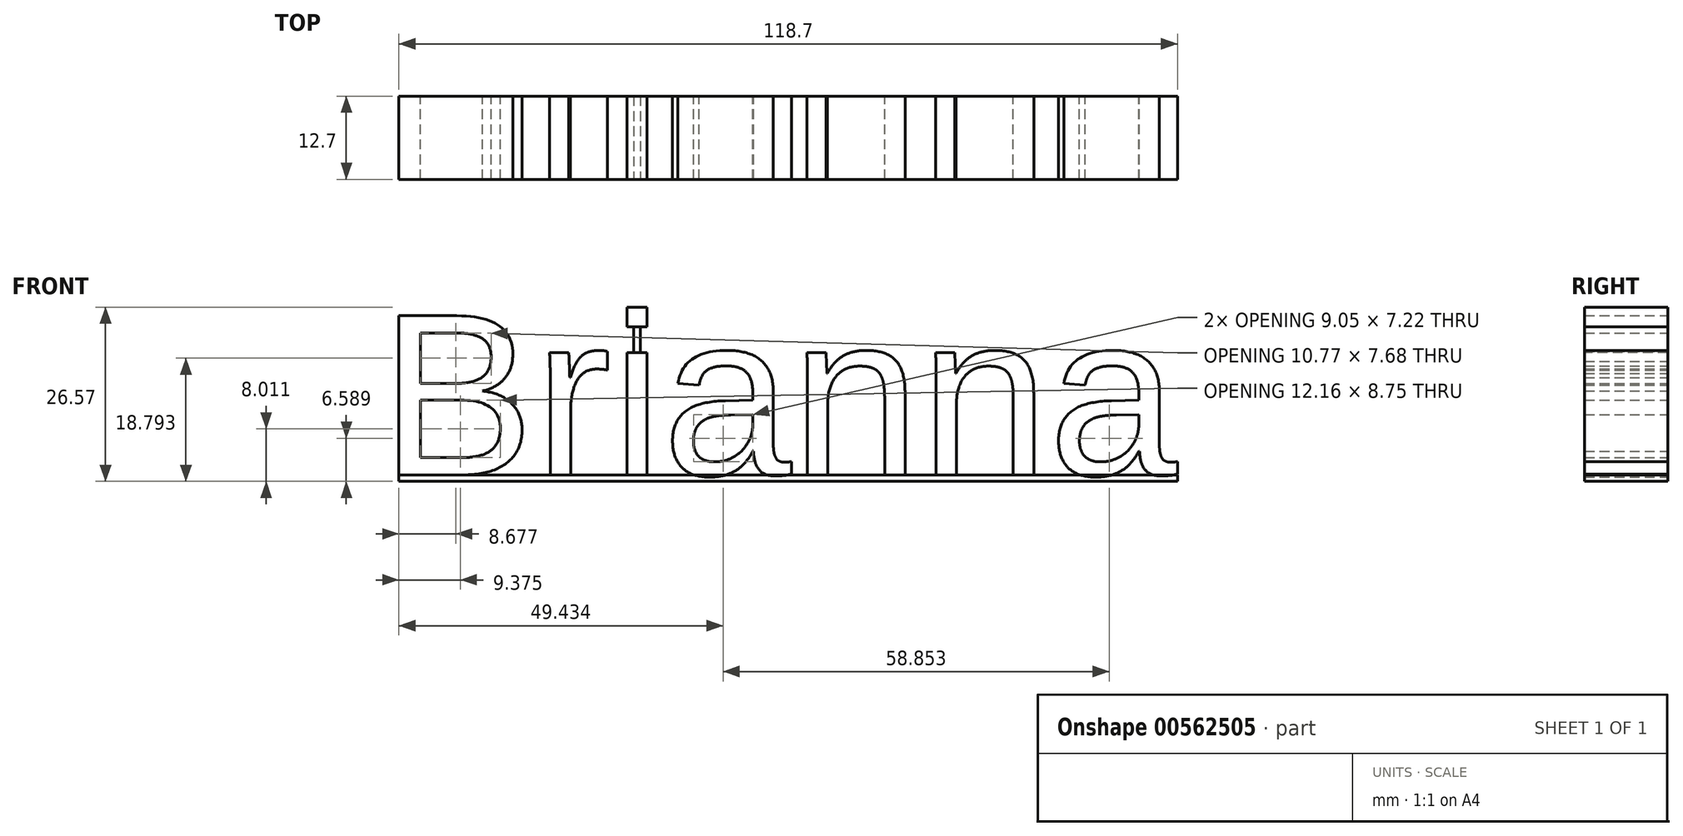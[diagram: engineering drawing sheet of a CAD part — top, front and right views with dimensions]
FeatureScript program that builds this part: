
annotation { "Feature Type Name" : "Feature", "Feature Type Description" : "" }
export const myFeature = defineFeature(function(context is Context, id is Id, definition is map)
    precondition{}
    {
        {
            var Q0;
            Q0=qCreatedBy(makeId("Front.planeOp"),FACE);
            var sketch = newSketch(context, id + "F0", { "sketchPlane" : qUnion([Q0])});
            skText(sketch, "E0", { "text": "Brianna", "fontName": "Arimo-Regular.ttf"});
            skPoint(sketch, "E1", {"position": v(0, 12.7) * mm});
            const initialGuessF0  = {"E0": [-0.06202, 0, 1, 0, 0.0254]};
            skSetInitialGuess(sketch, initialGuessF0);
            skSolve(sketch);
        }
        {
            var Q0;
            Q0=qSketchRegion(id+"F0",true);
            extrude(context, id + "F1", {"entities" : qUnion([Q0]), "endBound" : BoundingType.SYMMETRIC, "depth" : 12.7 * mm, "offsetDistance" : 25.4 * mm});
        }
        {
            var Q0;
            Q0=qCreatedBy(makeId("Top.planeOp"),FACE);
            var sketch = newSketch(context, id + "F2", { "sketchPlane" : qUnion([Q0])});
            skPoint(sketch, "E2.0", {"position": v(-59.12, 0) * mm});
            skLineSegment(sketch, "E3.0", {"start": v(-59.12, -6.35) * mm, "end": v(-59.12, 6.35) * mm});
            skLineSegment(sketch, "E4.0", {"start": v(59.57, -6.35) * mm, "end": v(59.57, 6.35) * mm});
            skLineSegment(sketch, "E5", {"start": v(-59.12, -6.35) * mm, "end": v(59.57, -6.35) * mm});
            skLineSegment(sketch, "E6", {"start": v(59.57, 6.35) * mm, "end": v(-59.12, 6.35) * mm});
            skSolve(sketch);
        }
        {
            var Q0;
            Q0=makeQuery(id+"F2.imprint","IMPRINT",FACE,{"disambiguationData":[TD([[makeQuery(id+"F2.imprint","IMPRINT",EDGE,{"derivedFrom":sQuery(id+"F2.wireOp",EDGE,"E3.0")}),-1.0]])]});
            extrude(context, id + "F3", {"entities" : qUnion([Q0]), "oppositeDirection" : true, "depth" : 1 * mm, "offsetDistance" : 25.4 * mm});
        }
        {
            var Q0;
            Q0=makeQuery(id+"F1.opExtrude","CAP_FACE",FACE,{"disambiguationData":[OSD([sQuery(id+"F0.wireOp",EDGE,"E0.sketch_text.stroke-41"),sQuery(id+"F0.wireOp",EDGE,"E0.sketch_text.stroke-42"),sQuery(id+"F0.wireOp",EDGE,"E0.sketch_text.stroke-43"),sQuery(id+"F0.wireOp",EDGE,"E0.sketch_text.stroke-44")])],"isStart":false});
            var sketch = newSketch(context, id + "F4", { "sketchPlane" : qUnion([Q0])});
            skPoint(sketch, "E7.0", {"position": v(-22.83, 22.6) * mm});
            skPoint(sketch, "E8.0", {"position": v(-22.83, 18.64) * mm});
            skLineSegment(sketch, "E9", {"start": v(-22.83, 22.6) * mm, "end": v(-22.83, 18.64) * mm, "construction": true});
            skLineSegment(sketch, "E10.bottom", {"start": v(-23.33, 22.6) * mm, "end": v(-22.33, 22.6) * mm});
            skLineSegment(sketch, "E10.top", {"start": v(-23.33, 18.64) * mm, "end": v(-22.33, 18.64) * mm});
            skLineSegment(sketch, "E10.left", {"start": v(-23.33, 22.6) * mm, "end": v(-23.33, 18.64) * mm});
            skLineSegment(sketch, "E10.right", {"start": v(-22.33, 22.6) * mm, "end": v(-22.33, 18.64) * mm});
            skSolve(sketch);
        }
        {
            var Q0;
            Q0 = qSketchRegion(id + "F4", true);
            var Q1;
            Q1=makeQuery(id+"F1.opExtrude","CAP_FACE",FACE,{"disambiguationData":[OSD([sQuery(id+"F0.wireOp",EDGE,"E0.sketch_text.stroke-37"),sQuery(id+"F0.wireOp",EDGE,"E0.sketch_text.stroke-38"),sQuery(id+"F0.wireOp",EDGE,"E0.sketch_text.stroke-39"),sQuery(id+"F0.wireOp",EDGE,"E0.sketch_text.stroke-40")])],"isStart":true});
            extrude(context, id + "F5", {"entities" : qUnion([Q0]), "endBound" : BoundingType.UP_TO_SURFACE, "oppositeDirection" : true, "depth" : 25.4 * mm, "endBoundEntityFace" : qUnion([Q1]), "offsetDistance" : 25.4 * mm});
        }
    });
